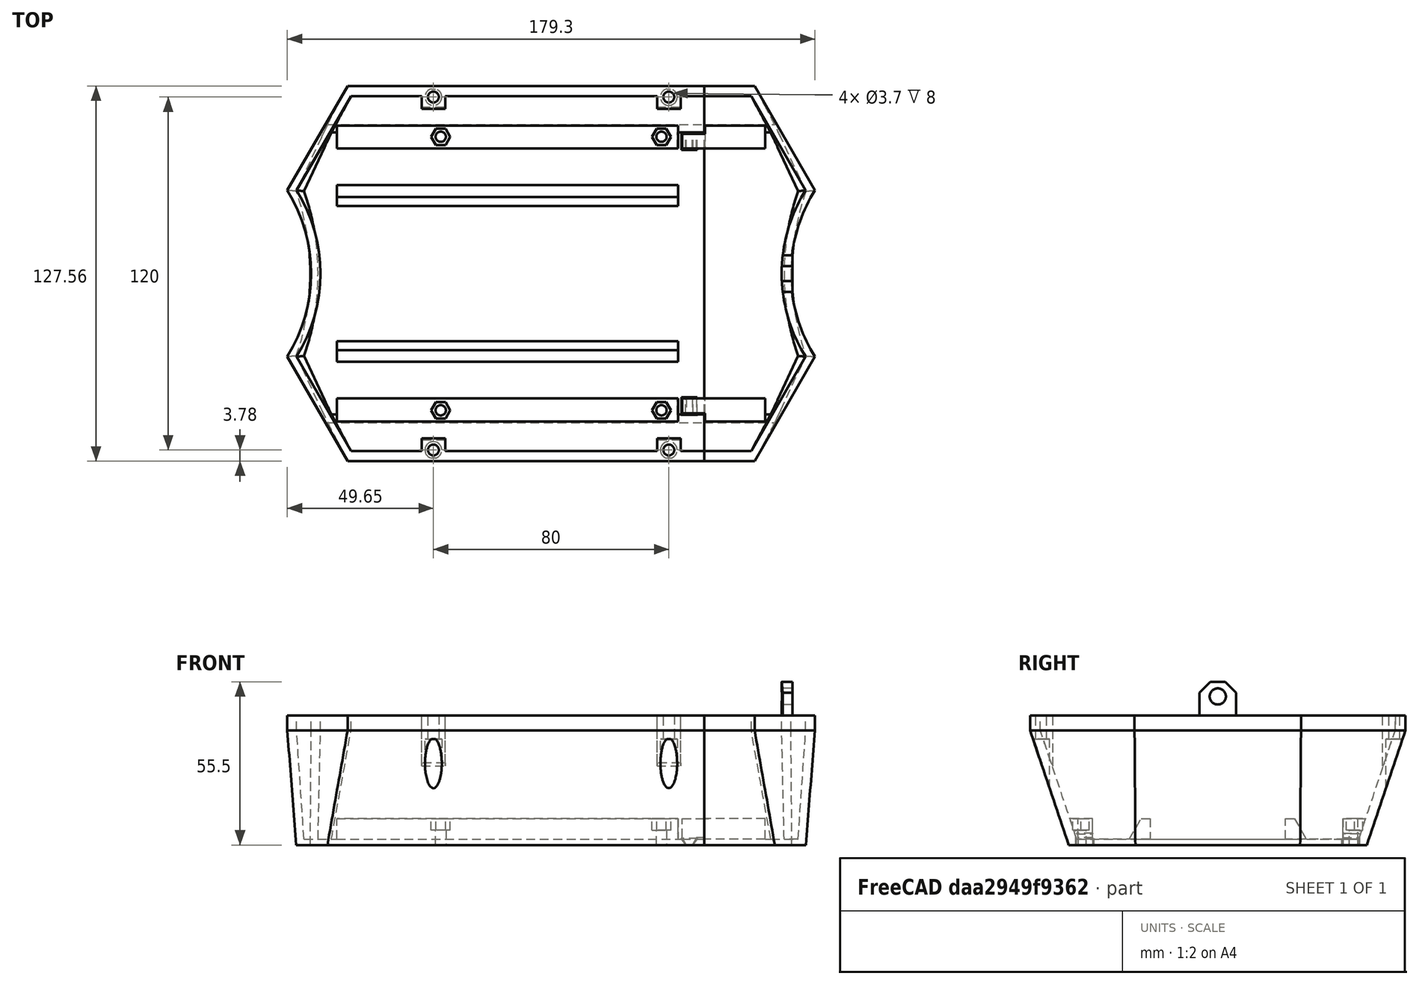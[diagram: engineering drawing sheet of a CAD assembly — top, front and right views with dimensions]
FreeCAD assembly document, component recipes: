
FREECAD ASSEMBLY — COMPONENT RECIPES ("sto56")

This assembly document has 2 components, labeled P0..P1 below (a component is one placed body or linked part). 0 of them carry a construction recipe — the FreeCAD feature program that regenerates the part from scratch, quoted from this document or its linked companion documents; the rest are supplied as boundary geometry only. No exploded tour is included for this assembly.
COMPONENT P0 — geometry summary ("Cut009010006006006005025008"; no construction recipe available for this part):
  bounding box: 179.3 x 127.6 x 55.5 mm
  tessellated surface: 7,472 triangles
  volume: 123800 mm^3 (10% of its bounding box)
  symmetry: mirror-symmetric across its y mid-plane
COMPONENT P1 — geometry summary ("Cube014"; no construction recipe available for this part):
  bounding box: 140.0 x 60.0 x 41.0 mm
  tessellated surface: 12 triangles
  volume: 344400 mm^3 (100% of its bounding box)
  symmetry: 2-fold rotationally symmetric about the y axis; 2-fold rotationally symmetric about the z axis
PROVENANCE & LICENSES
A FreeCAD (.FCStd) document from a public repository crawl; recipes are the document's own serialized feature recipes (and, for linked parts, companion documents' recipes).
License: as declared in the source repository (recorded in the dataset sidecar).
